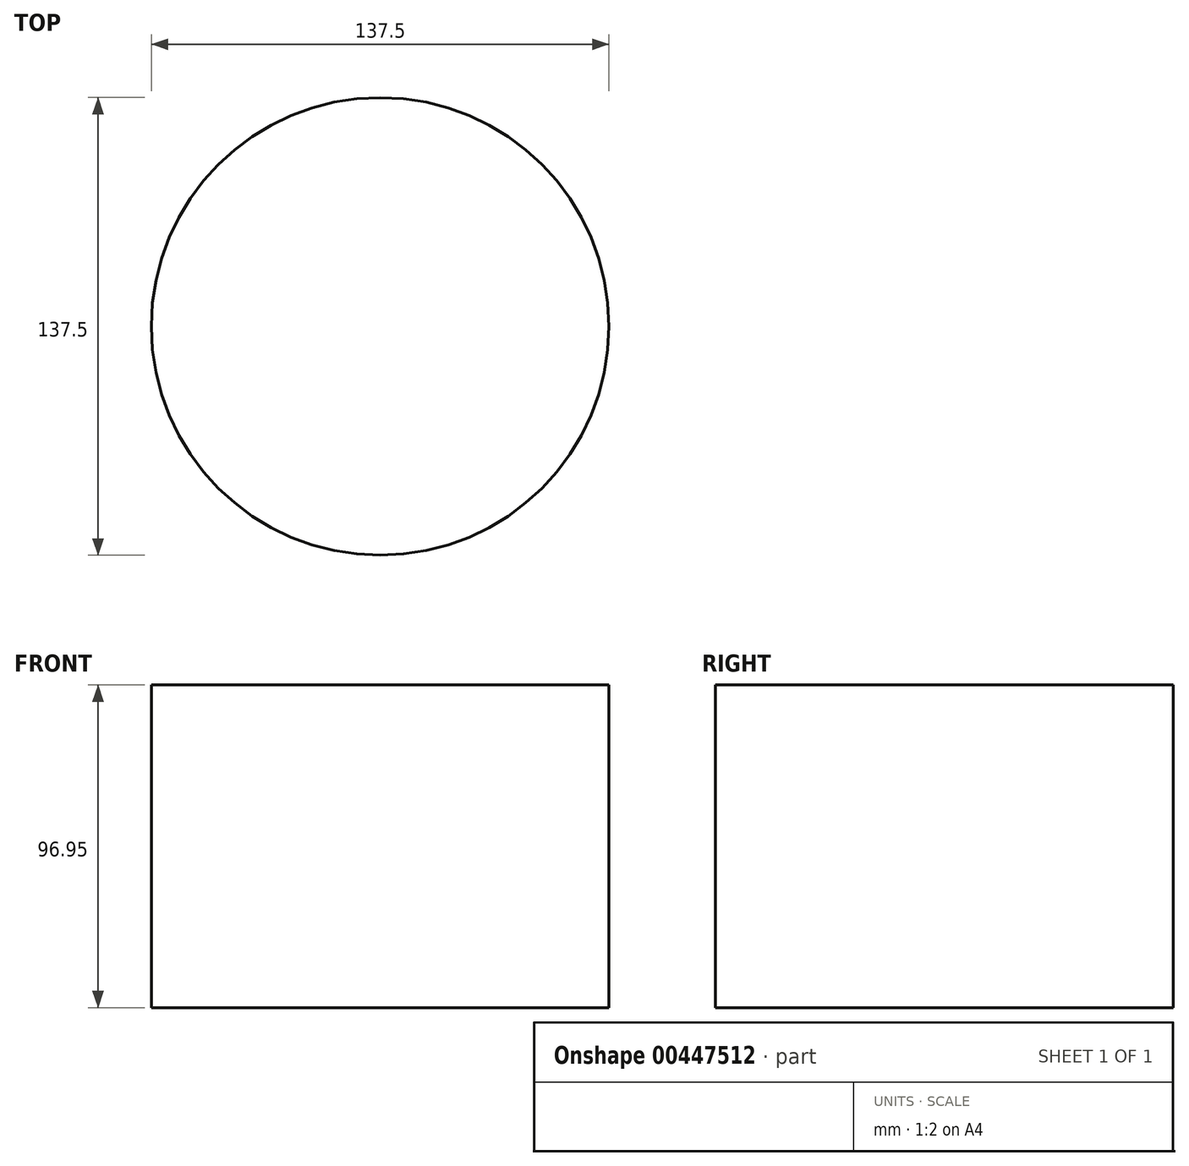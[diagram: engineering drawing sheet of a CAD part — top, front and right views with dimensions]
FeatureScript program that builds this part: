
annotation { "Feature Type Name" : "Feature", "Feature Type Description" : "" }
export const myFeature = defineFeature(function(context is Context, id is Id, definition is map)
    precondition{}
    {
        {
            var Q0;
            Q0=qCreatedBy(makeId("Top.planeOp"),FACE);
            var sketch = newSketch(context, id + "F0", { "sketchPlane" : qUnion([Q0])});
            skCircle(sketch, "E0", {"center": v(0, 0) * mm, "radius": 68.75 * mm});
            skSolve(sketch);
        }
        {
            var Q0;
            Q0=makeQuery(id+"F0.imprint","IMPRINT",FACE,{"disambiguationData":[TD([[makeQuery(id+"F0.imprint","IMPRINT",EDGE,{"derivedFrom":sQuery(id+"F0.wireOp",EDGE,"E0")}),1.0]])]});
            extrude(context, id + "F1", {"entities" : qUnion([Q0]), "depth" : 96.95 * mm});
        }
    });
